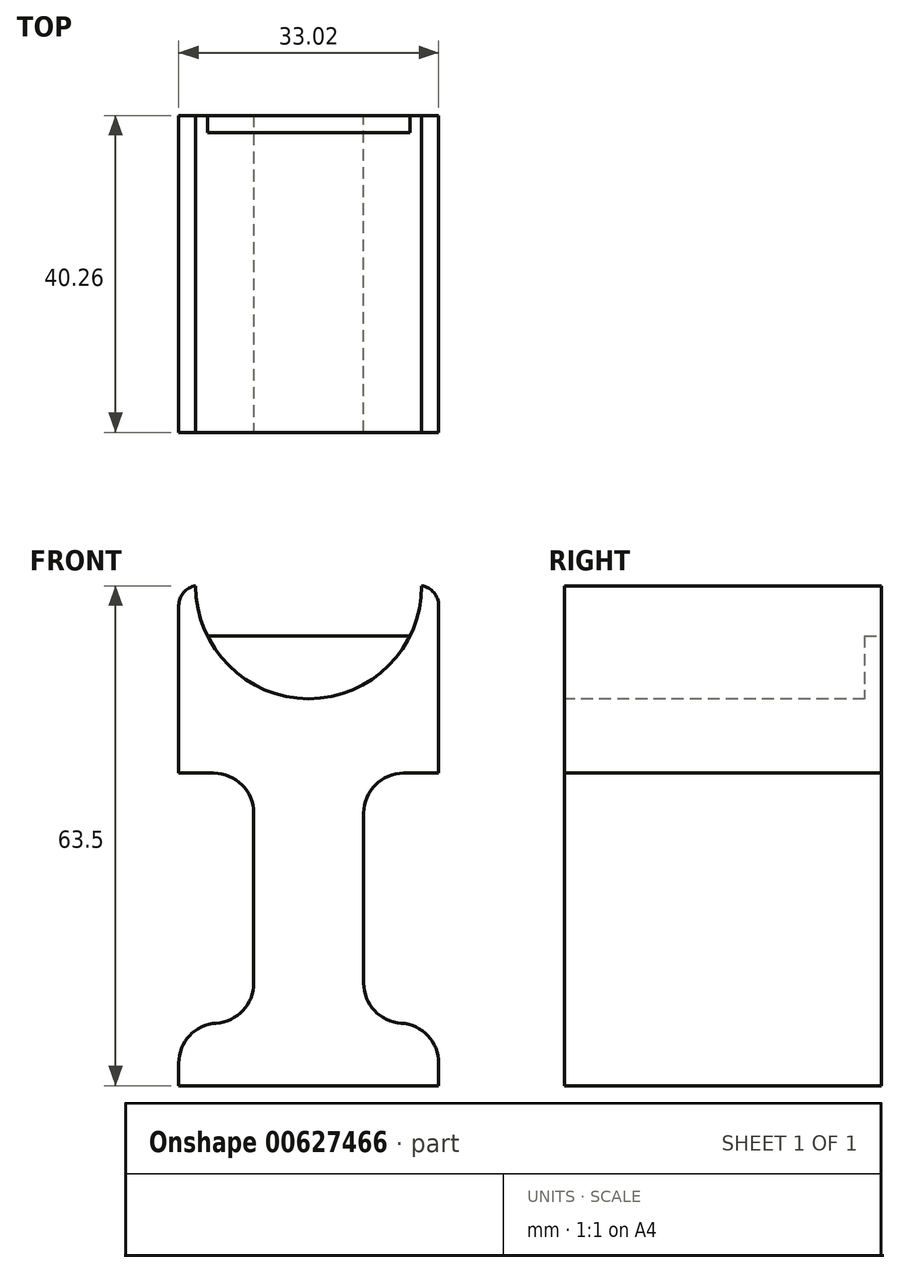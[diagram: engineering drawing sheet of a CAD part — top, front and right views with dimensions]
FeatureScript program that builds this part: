
annotation { "Feature Type Name" : "Feature", "Feature Type Description" : "" }
export const myFeature = defineFeature(function(context is Context, id is Id, definition is map)
    precondition{}
    {
        {
            var Q0;
            Q0=qCreatedBy(makeId("Top.planeOp"),FACE);
            var sketch = newSketch(context, id + "F0", { "sketchPlane" : qUnion([Q0])});
            skLineSegment(sketch, "E0.bottom", {"start": v(-17.34, 15.95) * mm, "end": v(15.68, 15.95) * mm});
            skLineSegment(sketch, "E0.top", {"start": v(-17.34, -24.31) * mm, "end": v(15.68, -24.31) * mm});
            skLineSegment(sketch, "E0.left", {"start": v(-17.34, 15.95) * mm, "end": v(-17.34, -24.31) * mm});
            skLineSegment(sketch, "E0.right", {"start": v(15.68, 15.95) * mm, "end": v(15.68, -24.31) * mm});
            skSolve(sketch);
        }
        {
            var Q0;
            Q0 = qSketchRegion(id + "F0", true);
            extrude(context, id + "F1", {"entities" : qUnion([Q0]), "depth" : 63.5 * mm, "offsetDistance" : 25.4 * mm});
        }
        {
            var Q0;
            Q0=makeQuery(id+"F1.opExtrude","SWEPT_FACE",FACE,{"disambiguationData":[OSD([sQuery(id+"F0.wireOp",EDGE,"E0.top")])]});
            var sketch = newSketch(context, id + "F2", { "sketchPlane" : qUnion([Q0])});
            skCircle(sketch, "E1", {"center": v(-0.83, 63.5) * mm, "radius": 14.35 * mm});
            skSolve(sketch);
        }
        {
            var Q0;
            Q0 = qSketchRegion(id + "F2", true);
            extrude(context, id + "F3", {"entities" : qUnion([Q0]), "operationType" : NewBodyOperationType.REMOVE, "oppositeDirection" : true, "depth" : 38.1 * mm, "offsetDistance" : 25.4 * mm});
        }
        {
            var Q0;
            Q0=makeQuery(id+"F1.opExtrude","SWEPT_FACE",FACE,{"disambiguationData":[OSD([sQuery(id+"F0.wireOp",EDGE,"E0.bottom")])]});
            var sketch = newSketch(context, id + "F4", { "sketchPlane" : qUnion([Q0])});
            skLineSegment(sketch, "E2", {"start": v(-13.53, 63.5) * mm, "end": v(15.18, 63.5) * mm});
            skArc(sketch, "E3", {"start": v(-13.53, 63.5) * mm, "mid": v(-13.15, 60.24) * mm, "end": v(-12.04, 57.15) * mm});
            skLineSegment(sketch, "E4", {"start": v(-12.04, 57.15) * mm, "end": v(13.7, 57.15) * mm});
            skArc(sketch, "E5.trimOffspring", {"start": v(13.7, 57.15) * mm, "mid": v(14.8, 60.24) * mm, "end": v(15.18, 63.5) * mm});
            skSolve(sketch);
        }
        {
            var Q0;
            Q0 = qSketchRegion(id + "F4", true);
            extrude(context, id + "F5", {"entities" : qUnion([Q0]), "operationType" : NewBodyOperationType.REMOVE, "oppositeDirection" : true, "depth" : 25.4 * mm, "offsetDistance" : 25.4 * mm});
        }
        {
            var Q0;
            Q0=makeQuery(id+"F1.opExtrude","CAP_EDGE",EDGE,{"disambiguationData":[OSD([sQuery(id+"F0.wireOp",EDGE,"E0.left")])],"isStart":false});
            var Q1;
            Q1=makeQuery(id+"F1.opExtrude","CAP_EDGE",EDGE,{"disambiguationData":[OSD([sQuery(id+"F0.wireOp",EDGE,"E0.right")])],"isStart":false});
            fillet(context, id + "F6", {"entities" : qUnion([Q0, Q1]), "radius" : 2.54 * mm, "tangentPropagation" : true, "allowEdgeOverflow" : false});
        }
        {
            var Q0;
            Q0=makeQuery(id+"F1.opExtrude","SWEPT_FACE",FACE,{"disambiguationData":[OSD([sQuery(id+"F0.wireOp",EDGE,"E0.top")])]});
            var sketch = newSketch(context, id + "F7", { "sketchPlane" : qUnion([Q0])});
            skLineSegment(sketch, "E6.bottom", {"start": v(-17.34, 39.7) * mm, "end": v(-7.81, 39.7) * mm});
            skLineSegment(sketch, "E6.top", {"start": v(-17.34, 7.95) * mm, "end": v(-7.81, 7.95) * mm});
            skLineSegment(sketch, "E6.left", {"start": v(-17.34, 39.7) * mm, "end": v(-17.34, 7.95) * mm});
            skLineSegment(sketch, "E6.right", {"start": v(-7.81, 39.7) * mm, "end": v(-7.81, 7.95) * mm});
            skLineSegment(sketch, "E7.bottom", {"start": v(15.68, 7.95) * mm, "end": v(6.16, 7.95) * mm});
            skLineSegment(sketch, "E7.top", {"start": v(15.68, 39.7) * mm, "end": v(6.16, 39.7) * mm});
            skLineSegment(sketch, "E7.left", {"start": v(15.68, 7.95) * mm, "end": v(15.68, 39.7) * mm});
            skLineSegment(sketch, "E7.right", {"start": v(6.16, 7.95) * mm, "end": v(6.16, 39.7) * mm});
            skSolve(sketch);
        }
        {
            var Q0;
            Q0 = qSketchRegion(id + "F7", true);
            extrude(context, id + "F8", {"entities" : qUnion([Q0]), "operationType" : NewBodyOperationType.REMOVE, "oppositeDirection" : true, "depth" : 50.8 * mm, "offsetDistance" : 25.4 * mm});
        }
        {
            var Q0;
            Q0=makeQuery(id+"F8.boolean.opBoolean","COPY",EDGE,{"derivedFrom":makeQuery(id+"F8.opExtrude","SWEPT_EDGE",EDGE,{"disambiguationData":[OSD([sQuery(id+"F0.wireOp",EDGE,"E0.top"),sQuery(id+"F0.wireOp",EDGE,"E0.left"),sQuery(id+"F7.wireOp",EDGE,"E6.bottom"),sQuery(id+"F7.wireOp",EDGE,"E6.left")])]})});
            var Q1;
            Q1=makeQuery(id+"F8.boolean.opBoolean","COPY",EDGE,{"derivedFrom":makeQuery(id+"F8.opExtrude","SWEPT_EDGE",EDGE,{"disambiguationData":[OSD([sQuery(id+"F0.wireOp",EDGE,"E0.top"),sQuery(id+"F0.wireOp",EDGE,"E0.left"),sQuery(id+"F7.wireOp",EDGE,"E6.top"),sQuery(id+"F7.wireOp",EDGE,"E6.left")])]})});
            var Q2;
            Q2=makeQuery(id+"F8.boolean.opBoolean","COPY",EDGE,{"derivedFrom":makeQuery(id+"F8.opExtrude","SWEPT_EDGE",EDGE,{"disambiguationData":[OSD([sQuery(id+"F0.wireOp",EDGE,"E0.top"),sQuery(id+"F0.wireOp",EDGE,"E0.right"),sQuery(id+"F7.wireOp",EDGE,"E7.bottom"),sQuery(id+"F7.wireOp",EDGE,"E7.left")])]})});
            var Q3;
            Q3=makeQuery(id+"F8.boolean.opBoolean","COPY",EDGE,{"derivedFrom":makeQuery(id+"F8.opExtrude","SWEPT_EDGE",EDGE,{"disambiguationData":[OSD([sQuery(id+"F0.wireOp",EDGE,"E0.top"),sQuery(id+"F0.wireOp",EDGE,"E0.right"),sQuery(id+"F7.wireOp",EDGE,"E7.top"),sQuery(id+"F7.wireOp",EDGE,"E7.left")])]})});
            fillet(context, id + "F9", {"entities" : qUnion([Q0, Q1, Q2, Q3]), "radius" : 5.08 * mm, "tangentPropagation" : true, "allowEdgeOverflow" : false});
        }
        {
            var Q0;
            Q0=makeQuery(id+"F8.boolean.opBoolean","COPY",EDGE,{"derivedFrom":makeQuery(id+"F8.opExtrude","SWEPT_EDGE",EDGE,{"disambiguationData":[OSD([sQuery(id+"F7.wireOp",EDGE,"E7.top"),sQuery(id+"F7.wireOp",EDGE,"E7.right")])]})});
            var Q1;
            Q1=makeQuery(id+"F8.boolean.opBoolean","COPY",EDGE,{"derivedFrom":makeQuery(id+"F8.opExtrude","SWEPT_EDGE",EDGE,{"disambiguationData":[OSD([sQuery(id+"F7.wireOp",EDGE,"E7.bottom"),sQuery(id+"F7.wireOp",EDGE,"E7.right")])]})});
            var Q2;
            Q2=makeQuery(id+"F8.boolean.opBoolean","COPY",EDGE,{"derivedFrom":makeQuery(id+"F8.opExtrude","SWEPT_EDGE",EDGE,{"disambiguationData":[OSD([sQuery(id+"F7.wireOp",EDGE,"E6.top"),sQuery(id+"F7.wireOp",EDGE,"E6.right")])]})});
            var Q3;
            Q3=makeQuery(id+"F8.boolean.opBoolean","COPY",EDGE,{"derivedFrom":makeQuery(id+"F8.opExtrude","SWEPT_EDGE",EDGE,{"disambiguationData":[OSD([sQuery(id+"F7.wireOp",EDGE,"E6.bottom"),sQuery(id+"F7.wireOp",EDGE,"E6.right")])]})});
            fillet(context, id + "F10", {"entities" : qUnion([Q0, Q1, Q2, Q3]), "radius" : 5.08 * mm, "tangentPropagation" : true, "allowEdgeOverflow" : false});
        }
    });
